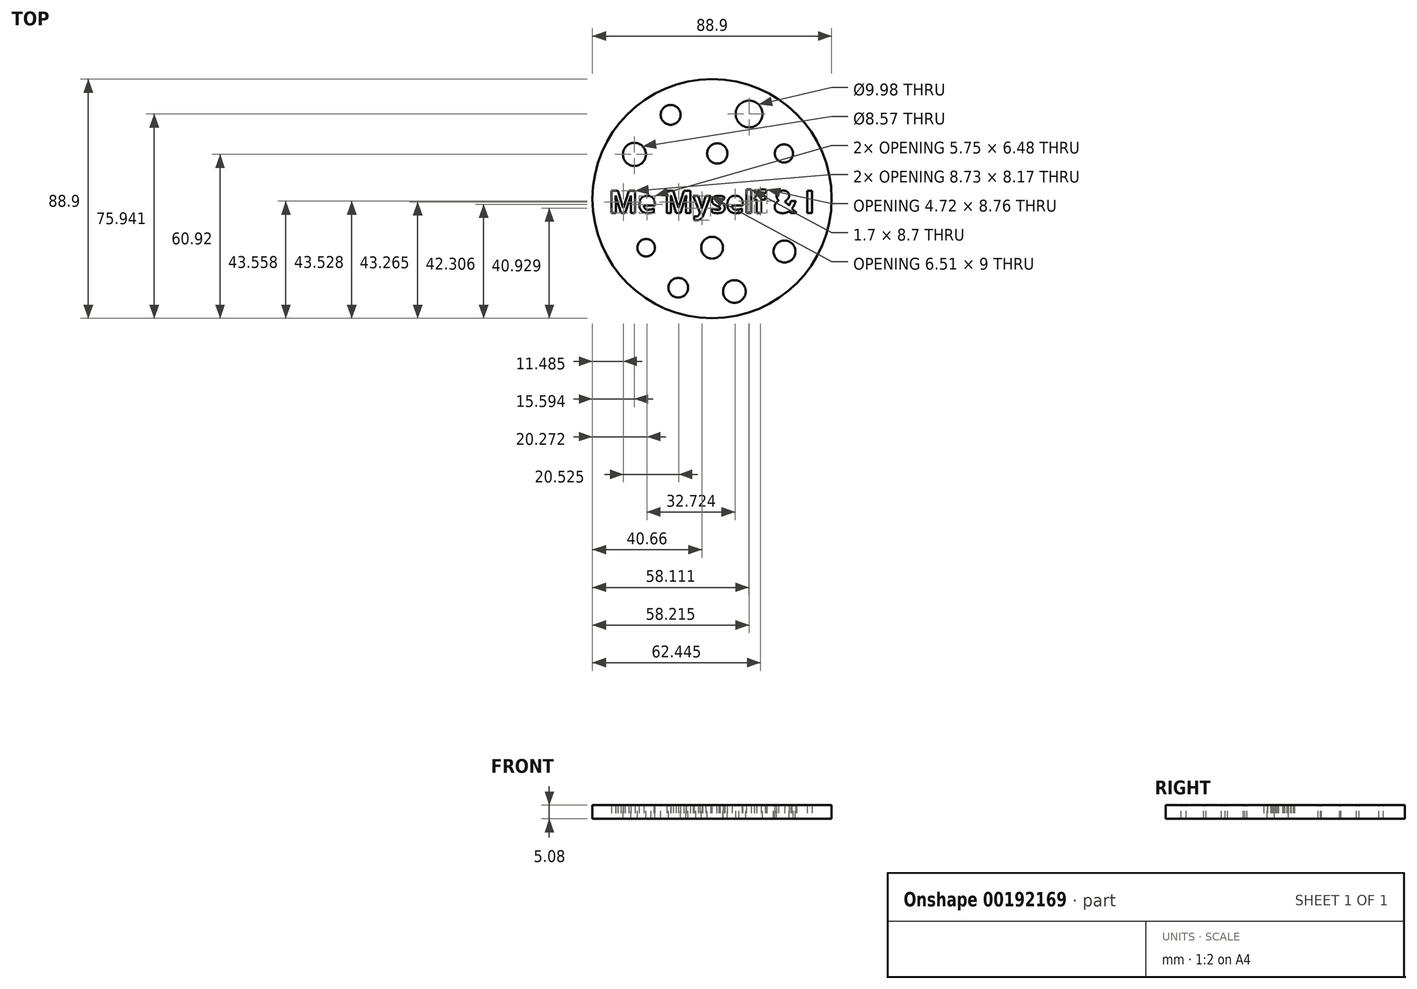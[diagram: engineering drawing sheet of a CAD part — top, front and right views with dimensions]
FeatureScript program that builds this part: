
annotation { "Feature Type Name" : "Feature", "Feature Type Description" : "" }
export const myFeature = defineFeature(function(context is Context, id is Id, definition is map)
    precondition{}
    {
        {
            var Q0;
            Q0=qCreatedBy(makeId("Top.planeOp"),FACE);
            var sketch = newSketch(context, id + "F0", { "sketchPlane" : qUnion([Q0])});
            skCircle(sketch, "E0", {"center": v(0, 0) * mm, "radius": 44.45 * mm});
            skText(sketch, "E1", { "text": "Me Myself & I", "fontName": "OpenSans-Bold.ttf"});
            const initialGuessF0  = {"E1": [-0.03836, -0.00527, 1, 0, 0.00824]};
            skSetInitialGuess(sketch, initialGuessF0);
            skSolve(sketch);
        }
        {
            var Q0;
            Q0=makeQuery(id+"F0.imprint","IMPRINT",FACE,{"disambiguationData":[TD([[makeQuery(id+"F0.imprint","IMPRINT",EDGE,{"derivedFrom":sQuery(id+"F0.wireOp",EDGE,"E0")}),1.0]])]});
            extrude(context, id + "F1", {"entities" : qUnion([Q0]), "endBound" : BoundingType.SYMMETRIC, "depth" : 5.08 * mm});
        }
        {
            var Q0;
            Q0=qCreatedBy(makeId("Top.planeOp"),FACE);
            var sketch = newSketch(context, id + "F2", { "sketchPlane" : qUnion([Q0])});
            skCircle(sketch, "E2", {"center": v(-15.4, 31.16) * mm, "radius": 3.68 * mm});
            skCircle(sketch, "E3", {"center": v(26.73, 16.82) * mm, "radius": 3.38 * mm});
            skCircle(sketch, "E4", {"center": v(-24.5, -18.23) * mm, "radius": 3.25 * mm});
            skCircle(sketch, "E5", {"center": v(-28.86, 16.47) * mm, "radius": 4.29 * mm});
            skCircle(sketch, "E6", {"center": v(13.77, 31.5) * mm, "radius": 4.99 * mm});
            skCircle(sketch, "E7", {"center": v(8.32, -34.51) * mm, "radius": 4.2 * mm});
            skCircle(sketch, "E8", {"center": v(26.9, -19.64) * mm, "radius": 4.08 * mm});
            skCircle(sketch, "E9", {"center": v(0, -18.23) * mm, "radius": 4.04 * mm});
            skCircle(sketch, "E10", {"center": v(1.95, 16.82) * mm, "radius": 3.76 * mm});
            skCircle(sketch, "E11", {"center": v(-12.57, -33.1) * mm, "radius": 3.65 * mm});
            skSolve(sketch);
        }
        {
            var Q0;
            Q0 = qSketchRegion(id + "F2", true);
            extrude(context, id + "F3", {"entities" : qUnion([Q0]), "operationType" : NewBodyOperationType.REMOVE, "oppositeDirection" : true, "depth" : 25.4 * mm});
        }
        {
            var Q0;
            Q0 = qSketchRegion(id + "F2", true);
            extrude(context, id + "F4", {"entities" : qUnion([Q0]), "operationType" : NewBodyOperationType.REMOVE, "depth" : 25.4 * mm});
        }
    });
